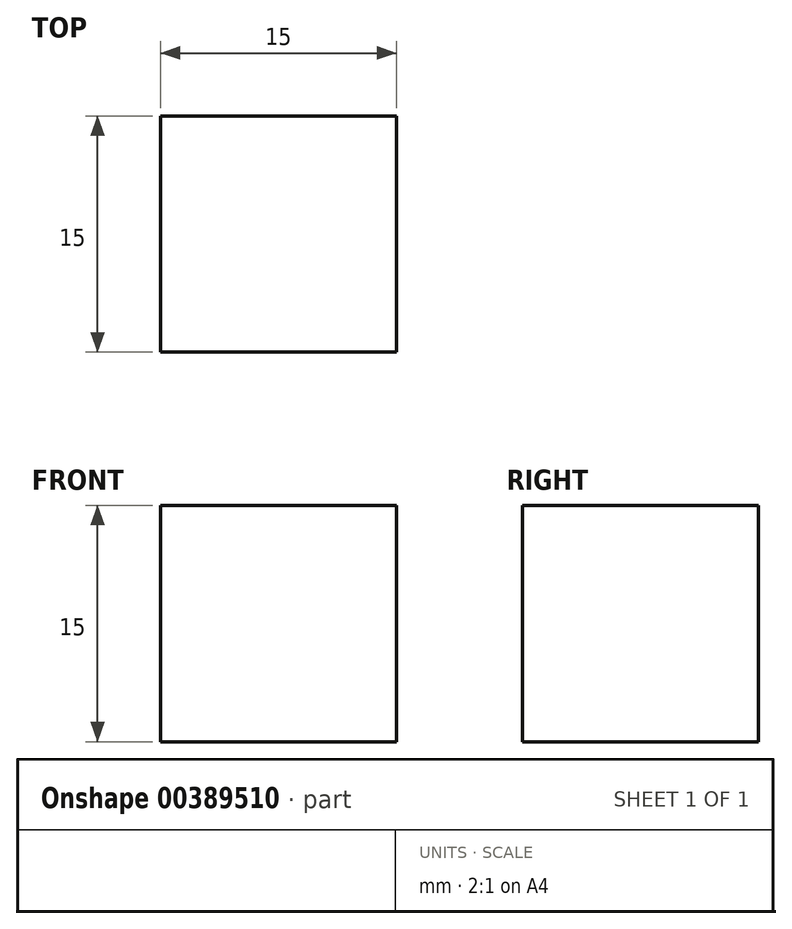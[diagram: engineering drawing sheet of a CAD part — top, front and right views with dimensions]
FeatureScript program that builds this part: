
annotation { "Feature Type Name" : "Feature", "Feature Type Description" : "" }
export const myFeature = defineFeature(function(context is Context, id is Id, definition is map)
    precondition{}
    {
        {
            var Q0;
            Q0=qCreatedBy(makeId("Top.planeOp"),FACE);
            var sketch = newSketch(context, id + "F0", { "sketchPlane" : qUnion([Q0])});
            skLineSegment(sketch, "E0", {"start": v(-34.61, 27.76) * mm, "end": v(-34.61, 12.76) * mm});
            skLineSegment(sketch, "E1", {"start": v(-19.61, 12.76) * mm, "end": v(-34.61, 12.76) * mm});
            skLineSegment(sketch, "E2", {"start": v(-19.61, 12.76) * mm, "end": v(-19.61, 27.76) * mm});
            skLineSegment(sketch, "E3", {"start": v(-19.61, 27.76) * mm, "end": v(-34.61, 27.76) * mm});
            skSolve(sketch);
        }
        {
            var Q0;
            Q0=makeQuery(id+"F0.imprint","IMPRINT",FACE,{"disambiguationData":[TD([[makeQuery(id+"F0.imprint","IMPRINT",EDGE,{"derivedFrom":sQuery(id+"F0.wireOp",EDGE,"E0")}),1.0]])]});
            extrude(context, id + "F1", {"entities" : qUnion([Q0]), "depth" : 15 * mm});
        }
    });
